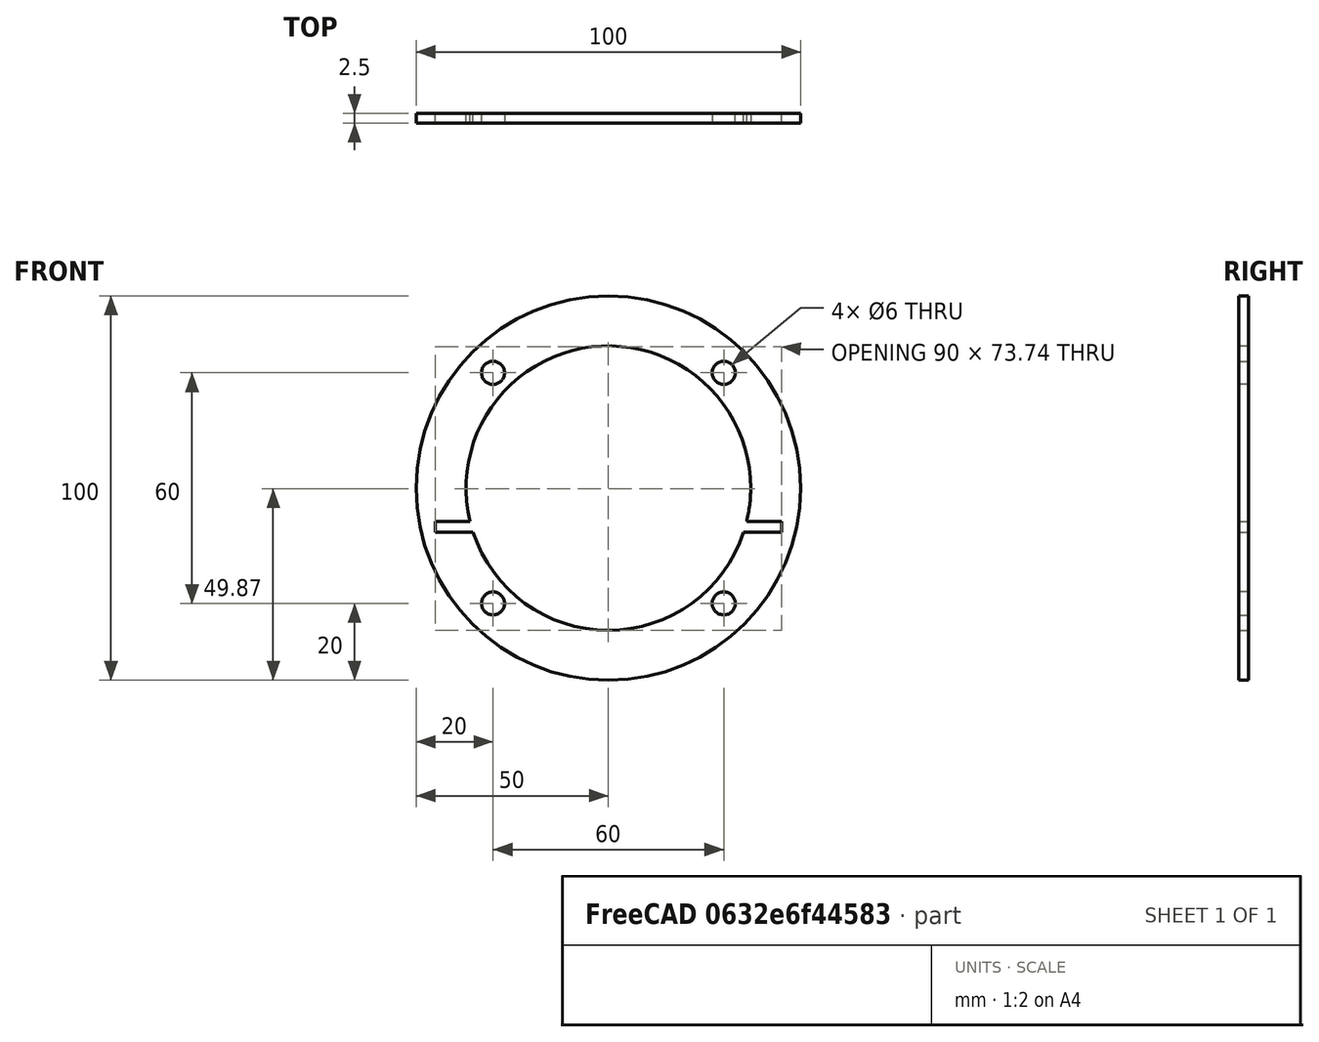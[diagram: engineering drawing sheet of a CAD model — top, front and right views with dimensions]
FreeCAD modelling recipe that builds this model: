
FCSTD DOCUMENT  (FreeCAD 0.20R29603 (Git))
Label: MechanicalCF35Mount005
License: All rights reserved
LicenseURL: http://en.wikipedia.org/wiki/All_rights_reserved
objects: Part::Cylinder×6, Part::Compound×5, Part::Box×2, Part::Cut×2, Part::MultiCommon×1, Part::Feature×1
note: 17 computed .brp shape members not serialized (recipe doc carries the construction recipe); baked Part::Feature solids carry a one-line shape summary decoded from their .brp

FEATURE [Part::Cylinder] Cylinder  label="Zylinder"
  Angle = 360
  AttacherType = Attacher::AttachEngine3D
  FirstAngle = 0
  Height = 317.7
  Placement = pos=(-30,12.7,-30) rot=(1,0,0;1.5708rad)
  Radius = 3
  SecondAngle = 0
FEATURE [Part::Cylinder] Cylinder001  label="Zylinder001"
  Angle = 360
  AttacherType = Attacher::AttachEngine3D
  FirstAngle = 0
  Height = 317.7
  Placement = pos=(-30,12.7,-30) rot=(1,0,0;1.5708rad)
  Radius = 3
  SecondAngle = 0
FEATURE [Part::Compound] Compound
  Links = -> [Cylinder001]
  Placement = pos=(0,0,0) rot=(0,1,0;1.5708rad)
FEATURE [Part::Cylinder] Cylinder002  label="Zylinder002"
  Angle = 360
  AttacherType = Attacher::AttachEngine3D
  FirstAngle = 0
  Height = 317.7
  Placement = pos=(-30,12.7,-30) rot=(1,0,0;1.5708rad)
  Radius = 3
  SecondAngle = 0
FEATURE [Part::Compound] Compound001
  Links = -> [Cylinder002]
  Placement = pos=(0,0,0) rot=(0,1,0;3.14159rad)
FEATURE [Part::Cylinder] Cylinder003  label="Zylinder003"
  Angle = 360
  AttacherType = Attacher::AttachEngine3D
  FirstAngle = 0
  Height = 317.7
  Placement = pos=(-30,12.7,-30) rot=(1,0,0;1.5708rad)
  Radius = 3
  SecondAngle = 0
FEATURE [Part::Compound] Compound002
  Links = -> [Cylinder003]
  Placement = pos=(0,0,0) rot=(0,-1,0;1.5708rad)
FEATURE [Part::Compound] Compound003  label="ThreadedRodsM6"
  Links = -> [Compound002,Compound,Compound001,Cylinder]
  Placement = pos=(0,20,0) rot=(0,0,1;0rad)
FEATURE [Part::Box] Box  label="Würfel"
  AttacherType = Attacher::AttachEngine3D
  Height = 2.8
  Length = 90
  Placement = pos=(-45,-10,-11.5) rot=(0,0,1;0rad)
  Width = 220
FEATURE [Part::Box] Box001  label="Würfel001"
  AttacherType = Attacher::AttachEngine3D
  Height = 100
  Length = 100
  Placement = pos=(-50,0,-50) rot=(0,0,1;0rad)
  Width = 2.5
FEATURE [Part::Compound] Compound004
  Links = -> [Compound003,Box]
FEATURE [Part::Cut] Cut
  Base = -> Box001
  Tool = -> Compound004
FEATURE [Part::Cylinder] Cylinder004  label="Zylinder004"
  Angle = 360
  AttacherType = Attacher::AttachEngine3D
  FirstAngle = 0
  Height = 10
  Placement = pos=(0,6,0) rot=(1,0,0;1.5708rad)
  Radius = 37
  SecondAngle = 0
FEATURE [Part::Cut] Cut001
  Base = -> Cut
  Tool = -> Cylinder004
FEATURE [Part::Cylinder] Cylinder005  label="Zylinder005"
  Angle = 360
  AttacherType = Attacher::AttachEngine3D
  FirstAngle = 0
  Height = 10
  Placement = pos=(0,6,0) rot=(1,0,0;1.5708rad)
  Radius = 50
  SecondAngle = 0
FEATURE [Part::MultiCommon] Common
  Shapes = -> [Cut001,Cylinder005]
FEATURE [Part::Feature] Common_solid  label="Common (Solid)"
  shape: bbox 100 x 2.5 x 100 mm, 19 faces (baked)
